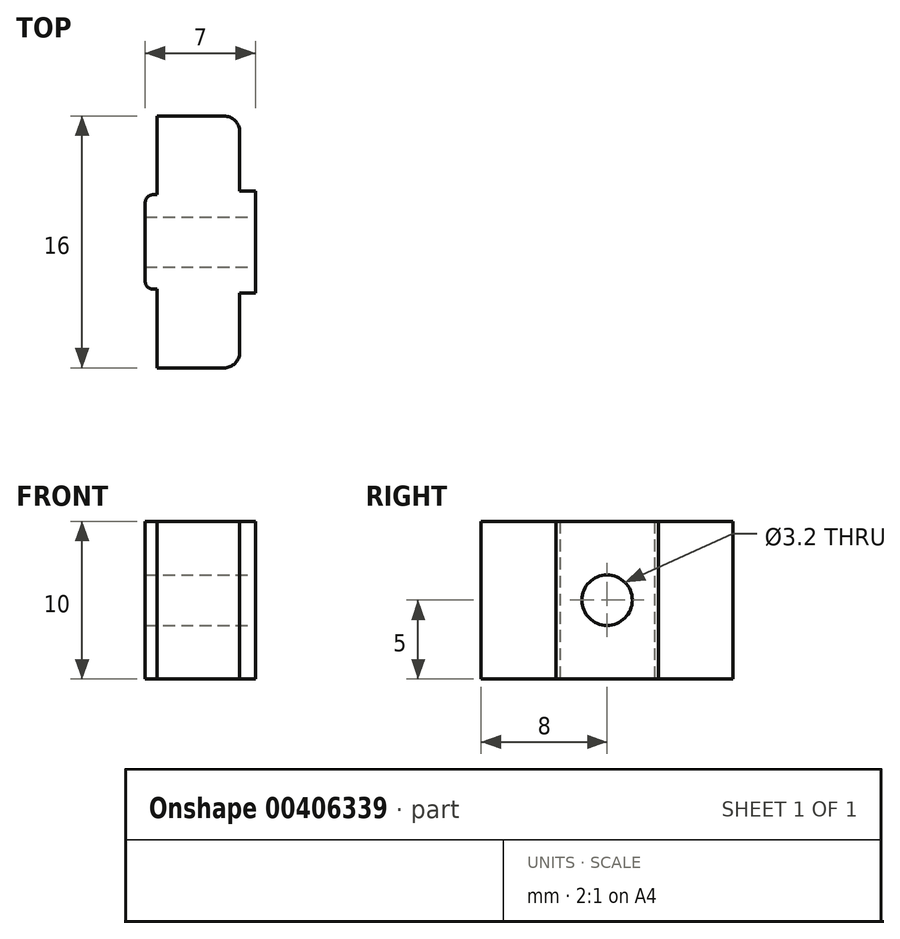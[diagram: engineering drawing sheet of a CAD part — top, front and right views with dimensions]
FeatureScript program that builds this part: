
annotation { "Feature Type Name" : "Feature", "Feature Type Description" : "" }
export const myFeature = defineFeature(function(context is Context, id is Id, definition is map)
    precondition{}
    {
        {
            var Q0;
            Q0=qCreatedBy(makeId("Top.planeOp"),FACE);
            var sketch = newSketch(context, id + "F0", { "sketchPlane" : qUnion([Q0])});
            skLineSegment(sketch, "E0.bottom", {"start": v(-0.75, 3) * mm, "end": v(0, 3) * mm});
            skLineSegment(sketch, "E0.top", {"start": v(-0.75, -3) * mm, "end": v(0, -3) * mm});
            skLineSegment(sketch, "E0.left", {"start": v(-0.75, 3) * mm, "end": v(-0.75, -3) * mm});
            skLineSegment(sketch, "E0.right", {"start": v(0, 3) * mm, "end": v(0, -3) * mm});
            skLineSegment(sketch, "E1.bottom", {"start": v(0, 8) * mm, "end": v(5.25, 8) * mm});
            skLineSegment(sketch, "E1.top", {"start": v(0, -8) * mm, "end": v(5.25, -8) * mm});
            skLineSegment(sketch, "E1.left", {"start": v(0, 8) * mm, "end": v(0, -8) * mm});
            skLineSegment(sketch, "E1.right", {"start": v(5.25, 8) * mm, "end": v(5.25, -8) * mm});
            skSolve(sketch);
        }
        {
            var Q0;
            {var subQ0=sQuery(id+"F0.wireOp",EDGE,"E0.bottom");Q0=makeQuery(id+"F0.imprint","IMPRINT",FACE,{"disambiguationData":[TD([[makeQuery(id+"F0.imprint","IMPRINT",EDGE,{"derivedFrom":subQ0}),-1.0]])]});}
            var Q1;
            {var subQ3=sQuery(id+"F0.wireOp",EDGE,"E1.bottom");Q1=makeQuery(id+"F0.imprint","IMPRINT",FACE,{"disambiguationData":[TD([[makeQuery(id+"F0.imprint","IMPRINT",EDGE,{"derivedFrom":subQ3}),-1.0]])]});}
            extrude(context, id + "F1", {"entities" : qUnion([Q0, Q1]), "depth" : 10 * mm});
        }
        {
            var Q0;
            Q0=makeQuery(id+"F1.opExtrude","SWEPT_FACE",FACE,{"disambiguationData":[OSD([sQuery(id+"F0.wireOp",EDGE,"E1.right")])]});
            var sketch = newSketch(context, id + "F2", { "sketchPlane" : qUnion([Q0])});
            skCircle(sketch, "E2", {"center": v(0, 5) * mm, "radius": 3.25 * mm});
            skPoint(sketch, "E2.centerSnap0", {"position": v(0, 10) * mm});
            skPoint(sketch, "E2.centerSnap1", {"position": v(8, 5) * mm});
            skCircle(sketch, "E3", {"center": v(0, 5) * mm, "radius": 1.6 * mm});
            skLineSegment(sketch, "E4.bottom", {"start": v(3.25, 10) * mm, "end": v(-3.25, 10) * mm});
            skLineSegment(sketch, "E4.top", {"start": v(3.25, 0) * mm, "end": v(-3.25, 0) * mm});
            skLineSegment(sketch, "E4.left", {"start": v(3.25, 10) * mm, "end": v(3.25, 0) * mm});
            skLineSegment(sketch, "E4.right", {"start": v(-3.25, 10) * mm, "end": v(-3.25, 0) * mm});
            skSolve(sketch);
        }
        {
            var Q0;
            Q0=makeQuery(id+"F2.imprint","IMPRINT",FACE,{"disambiguationData":[TD([[makeQuery(id+"F2.imprint","IMPRINT",EDGE,{"derivedFrom":sQuery(id+"F2.wireOp",EDGE,"E3")}),1.0]])]});
            extrude(context, id + "F3", {"entities" : qUnion([Q0]), "operationType" : NewBodyOperationType.REMOVE, "oppositeDirection" : true, "depth" : 25 * mm});
        }
        {
            var Q0;
            {var subQ5=sQuery(id+"F2.wireOp",EDGE,"E4.bottom");Q0=makeQuery(id+"F2.imprint","IMPRINT",FACE,{"disambiguationData":[TD([[makeQuery(id+"F2.imprint","IMPRINT",EDGE,{"derivedFrom":subQ5}),1.0]])]});}
            var Q1;
            Q1=makeQuery(id+"F2.imprint","IMPRINT",FACE,{"disambiguationData":[TD([[makeQuery(id+"F2.imprint","IMPRINT",EDGE,{"derivedFrom":sQuery(id+"F2.wireOp",EDGE,"E3")}),-1.0]])]});
            var Q2;
            {var subQ5=sQuery(id+"F2.wireOp",EDGE,"E4.top");Q2=makeQuery(id+"F2.imprint","IMPRINT",FACE,{"disambiguationData":[TD([[makeQuery(id+"F2.imprint","IMPRINT",EDGE,{"derivedFrom":subQ5}),-1.0]])]});}
            extrude(context, id + "F4", {"entities" : qUnion([Q0, Q1, Q2]), "operationType" : NewBodyOperationType.ADD, "depth" : 1 * mm});
        }
        {
            var Q0;
            Q0=makeQuery(id+"F1.opExtrude","SWEPT_EDGE",EDGE,{"disambiguationData":[OSD([sQuery(id+"F0.wireOp",EDGE,"E1.top"),sQuery(id+"F0.wireOp",EDGE,"E1.right")])]});
            var Q1;
            Q1=makeQuery(id+"F1.opExtrude","SWEPT_EDGE",EDGE,{"disambiguationData":[OSD([sQuery(id+"F0.wireOp",EDGE,"E1.bottom"),sQuery(id+"F0.wireOp",EDGE,"E1.right")])]});
            fillet(context, id + "F5", {"entities" : qUnion([Q0, Q1]), "radius" : 1 * mm, "tangentPropagation" : true, "allowEdgeOverflow" : false});
        }
        {
            var Q0;
            Q0=makeQuery(id+"F1.opExtrude","SWEPT_EDGE",EDGE,{"disambiguationData":[OSD([sQuery(id+"F0.wireOp",EDGE,"E0.top"),sQuery(id+"F0.wireOp",EDGE,"E0.left")])]});
            var Q1;
            Q1=makeQuery(id+"F1.opExtrude","SWEPT_EDGE",EDGE,{"disambiguationData":[OSD([sQuery(id+"F0.wireOp",EDGE,"E0.bottom"),sQuery(id+"F0.wireOp",EDGE,"E0.left")])]});
            fillet(context, id + "F6", {"entities" : qUnion([Q0, Q1]), "radius" : 0.5 * mm, "tangentPropagation" : true, "allowEdgeOverflow" : false});
        }
    });
